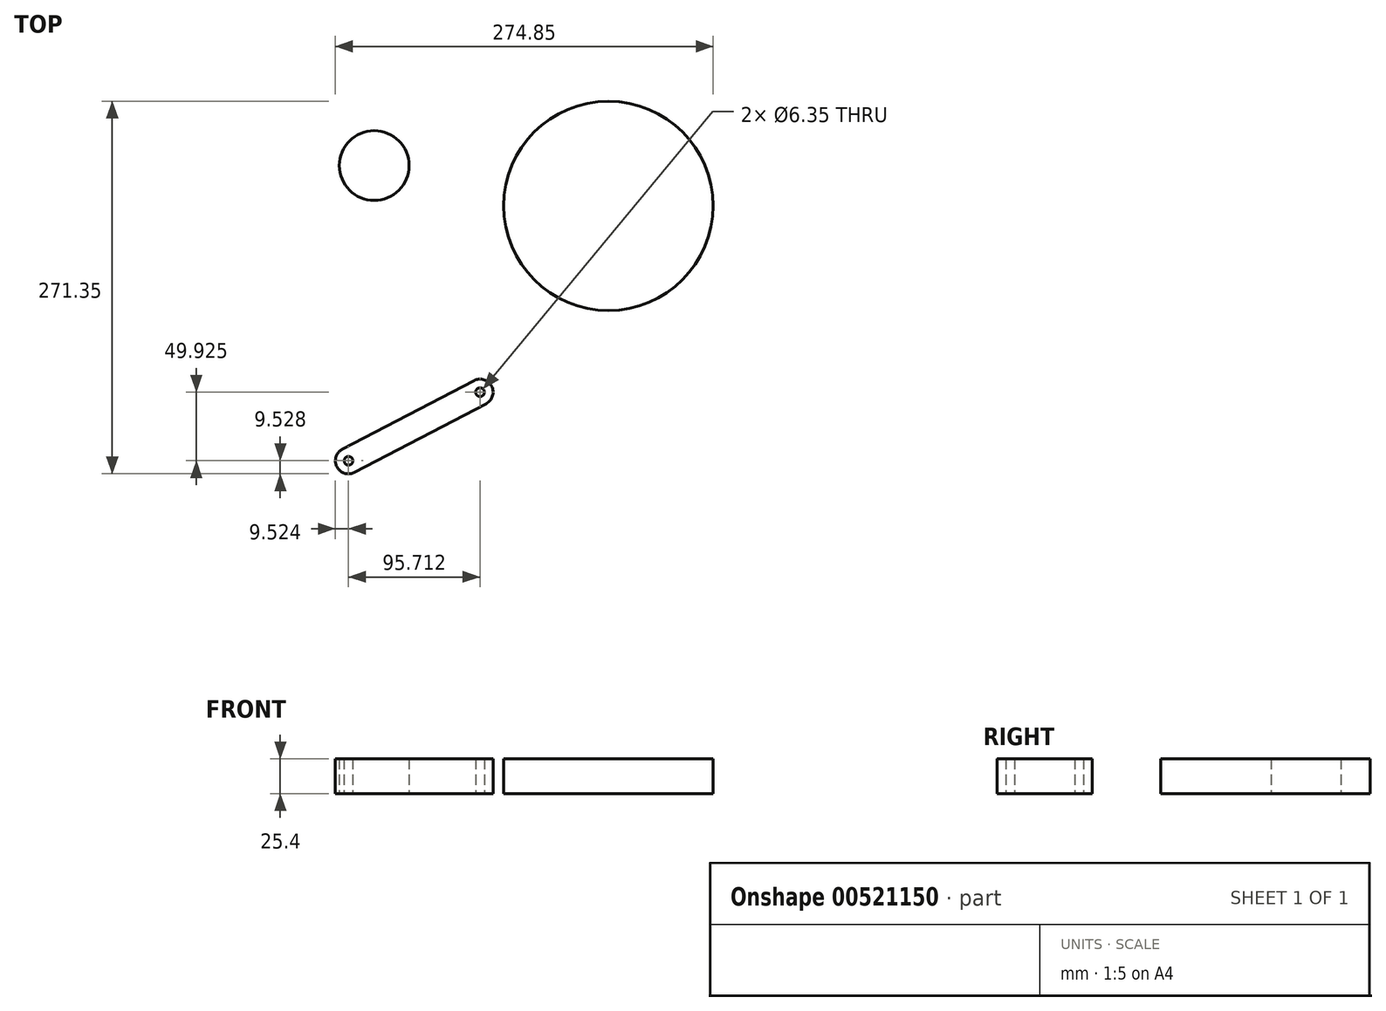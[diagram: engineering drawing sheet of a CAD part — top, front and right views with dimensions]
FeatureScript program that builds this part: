
annotation { "Feature Type Name" : "Feature", "Feature Type Description" : "" }
export const myFeature = defineFeature(function(context is Context, id is Id, definition is map)
    precondition{}
    {
        {
            var Q0;
            Q0=qCreatedBy(makeId("Top.planeOp"),FACE);
            var sketch = newSketch(context, id + "F0", { "sketchPlane" : qUnion([Q0])});
            skCircle(sketch, "E0", {"center": v(0, 0) * mm, "radius": 76.2 * mm});
            skArc(sketch, "E1", {"start": v(-14, 74.9) * mm, "mid": v(-8.35, 82.13) * mm, "end": v(-1.37, 76.19) * mm});
            skArc(sketch, "E2.1.0", {"start": v(-36.45, 66.92) * mm, "mid": v(-33.32, 75.53) * mm, "end": v(-24.84, 72.04) * mm});
            skArc(sketch, "E2.2.0", {"start": v(-55.35, 52.38) * mm, "mid": v(-55.03, 61.54) * mm, "end": v(-45.89, 60.83) * mm});
            skArc(sketch, "E3.2.3.0", {"start": v(-68.82, 32.7) * mm, "mid": v(-71.35, 41.52) * mm, "end": v(-62.44, 43.68) * mm});
            skArc(sketch, "E3.2.4.0", {"start": v(-75.56, 9.84) * mm, "mid": v(-80.69, 17.44) * mm, "end": v(-72.88, 22.24) * mm});
            skArc(sketch, "E3.2.5.0", {"start": v(-74.9, -14) * mm, "mid": v(-82.13, -8.35) * mm, "end": v(-76.19, -1.37) * mm});
            skArc(sketch, "E3.2.6.0", {"start": v(-66.92, -36.45) * mm, "mid": v(-75.53, -33.32) * mm, "end": v(-72.04, -24.84) * mm});
            skArc(sketch, "E3.2.7.0", {"start": v(-52.38, -55.35) * mm, "mid": v(-61.54, -55.03) * mm, "end": v(-60.83, -45.89) * mm});
            skArc(sketch, "E3.2.8.0", {"start": v(-32.7, -68.82) * mm, "mid": v(-41.52, -71.35) * mm, "end": v(-43.68, -62.44) * mm});
            skArc(sketch, "E3.2.9.0", {"start": v(-9.84, -75.56) * mm, "mid": v(-17.44, -80.69) * mm, "end": v(-22.24, -72.88) * mm});
            skArc(sketch, "E4.2.10.0", {"start": v(14, -74.9) * mm, "mid": v(8.35, -82.13) * mm, "end": v(1.37, -76.19) * mm});
            skArc(sketch, "E4.2.11.0", {"start": v(36.45, -66.92) * mm, "mid": v(33.32, -75.53) * mm, "end": v(24.84, -72.04) * mm});
            skArc(sketch, "E4.2.12.0", {"start": v(55.35, -52.38) * mm, "mid": v(55.03, -61.54) * mm, "end": v(45.89, -60.83) * mm});
            skArc(sketch, "E4.2.13.0", {"start": v(68.82, -32.7) * mm, "mid": v(71.35, -41.52) * mm, "end": v(62.44, -43.68) * mm});
            skArc(sketch, "E4.2.14.0", {"start": v(75.56, -9.84) * mm, "mid": v(80.69, -17.44) * mm, "end": v(72.88, -22.24) * mm});
            skArc(sketch, "E4.2.15.0", {"start": v(74.9, 14) * mm, "mid": v(82.13, 8.35) * mm, "end": v(76.19, 1.37) * mm});
            skArc(sketch, "E4.2.16.0", {"start": v(66.92, 36.45) * mm, "mid": v(75.53, 33.32) * mm, "end": v(72.04, 24.84) * mm});
            skArc(sketch, "E4.2.17.0", {"start": v(52.38, 55.35) * mm, "mid": v(61.54, 55.03) * mm, "end": v(60.83, 45.89) * mm});
            skArc(sketch, "E4.2.18.0", {"start": v(32.7, 68.82) * mm, "mid": v(41.52, 71.35) * mm, "end": v(43.68, 62.44) * mm});
            skArc(sketch, "E4.2.19.0", {"start": v(9.84, 75.56) * mm, "mid": v(17.44, 80.69) * mm, "end": v(22.24, 72.88) * mm});
            skSolve(sketch);
        }
        {
            var Q0;
            {var subQ1=sQuery(id+"F0.wireOp",EDGE,"E0");var subQ26=sQuery(id+"F0.wireOp",EDGE,"E4.2.15.0");var subQ27=makeQuery(id+"F0.imprint","INTERSECT",VERTEX,{"disambiguationData":[OD(0.0)],"derivedFrom":[subQ1,subQ26]});Q0=makeQuery(id+"F0.imprint","IMPRINT",FACE,{"disambiguationData":[TD([[makeQuery(id+"F0.imprint","IMPRINT",EDGE,{"disambiguationData":[TD([[subQ27,1.0]])],"derivedFrom":subQ1}),1.0]])]});}
            var Q1;
            {var subQ0=sQuery(id+"F0.wireOp",EDGE,"E2.2.0");Q1=makeQuery(id+"F0.imprint","IMPRINT",FACE,{"disambiguationData":[TD([[makeQuery(id+"F0.imprint","IMPRINT",EDGE,{"derivedFrom":subQ0}),-1.0]])]});}
            var Q2;
            {var subQ0=sQuery(id+"F0.wireOp",EDGE,"E3.2.3.0");Q2=makeQuery(id+"F0.imprint","IMPRINT",FACE,{"disambiguationData":[TD([[makeQuery(id+"F0.imprint","IMPRINT",EDGE,{"derivedFrom":subQ0}),-1.0]])]});}
            var Q3;
            {var subQ0=sQuery(id+"F0.wireOp",EDGE,"E3.2.4.0");Q3=makeQuery(id+"F0.imprint","IMPRINT",FACE,{"disambiguationData":[TD([[makeQuery(id+"F0.imprint","IMPRINT",EDGE,{"derivedFrom":subQ0}),-1.0]])]});}
            var Q4;
            {var subQ0=sQuery(id+"F0.wireOp",EDGE,"E3.2.5.0");Q4=makeQuery(id+"F0.imprint","IMPRINT",FACE,{"disambiguationData":[TD([[makeQuery(id+"F0.imprint","IMPRINT",EDGE,{"derivedFrom":subQ0}),-1.0]])]});}
            var Q5;
            {var subQ0=sQuery(id+"F0.wireOp",EDGE,"E3.2.6.0");Q5=makeQuery(id+"F0.imprint","IMPRINT",FACE,{"disambiguationData":[TD([[makeQuery(id+"F0.imprint","IMPRINT",EDGE,{"derivedFrom":subQ0}),-1.0]])]});}
            var Q6;
            {var subQ0=sQuery(id+"F0.wireOp",EDGE,"E3.2.7.0");Q6=makeQuery(id+"F0.imprint","IMPRINT",FACE,{"disambiguationData":[TD([[makeQuery(id+"F0.imprint","IMPRINT",EDGE,{"derivedFrom":subQ0}),-1.0]])]});}
            var Q7;
            {var subQ0=sQuery(id+"F0.wireOp",EDGE,"E3.2.8.0");Q7=makeQuery(id+"F0.imprint","IMPRINT",FACE,{"disambiguationData":[TD([[makeQuery(id+"F0.imprint","IMPRINT",EDGE,{"derivedFrom":subQ0}),-1.0]])]});}
            var Q8;
            {var subQ0=sQuery(id+"F0.wireOp",EDGE,"E3.2.9.0");Q8=makeQuery(id+"F0.imprint","IMPRINT",FACE,{"disambiguationData":[TD([[makeQuery(id+"F0.imprint","IMPRINT",EDGE,{"derivedFrom":subQ0}),-1.0]])]});}
            var Q9;
            {var subQ0=sQuery(id+"F0.wireOp",EDGE,"E4.2.10.0");Q9=makeQuery(id+"F0.imprint","IMPRINT",FACE,{"disambiguationData":[TD([[makeQuery(id+"F0.imprint","IMPRINT",EDGE,{"derivedFrom":subQ0}),-1.0]])]});}
            var Q10;
            {var subQ0=sQuery(id+"F0.wireOp",EDGE,"E4.2.11.0");Q10=makeQuery(id+"F0.imprint","IMPRINT",FACE,{"disambiguationData":[TD([[makeQuery(id+"F0.imprint","IMPRINT",EDGE,{"derivedFrom":subQ0}),-1.0]])]});}
            var Q11;
            {var subQ0=sQuery(id+"F0.wireOp",EDGE,"E4.2.12.0");Q11=makeQuery(id+"F0.imprint","IMPRINT",FACE,{"disambiguationData":[TD([[makeQuery(id+"F0.imprint","IMPRINT",EDGE,{"derivedFrom":subQ0}),-1.0]])]});}
            var Q12;
            {var subQ0=sQuery(id+"F0.wireOp",EDGE,"E4.2.13.0");Q12=makeQuery(id+"F0.imprint","IMPRINT",FACE,{"disambiguationData":[TD([[makeQuery(id+"F0.imprint","IMPRINT",EDGE,{"derivedFrom":subQ0}),-1.0]])]});}
            var Q13;
            {var subQ0=sQuery(id+"F0.wireOp",EDGE,"E4.2.14.0");Q13=makeQuery(id+"F0.imprint","IMPRINT",FACE,{"disambiguationData":[TD([[makeQuery(id+"F0.imprint","IMPRINT",EDGE,{"derivedFrom":subQ0}),-1.0]])]});}
            var Q14;
            {var subQ0=sQuery(id+"F0.wireOp",EDGE,"E4.2.15.0");Q14=makeQuery(id+"F0.imprint","IMPRINT",FACE,{"disambiguationData":[TD([[makeQuery(id+"F0.imprint","IMPRINT",EDGE,{"derivedFrom":subQ0}),-1.0]])]});}
            var Q15;
            {var subQ0=sQuery(id+"F0.wireOp",EDGE,"E4.2.16.0");Q15=makeQuery(id+"F0.imprint","IMPRINT",FACE,{"disambiguationData":[TD([[makeQuery(id+"F0.imprint","IMPRINT",EDGE,{"derivedFrom":subQ0}),-1.0]])]});}
            var Q16;
            {var subQ0=sQuery(id+"F0.wireOp",EDGE,"E4.2.17.0");Q16=makeQuery(id+"F0.imprint","IMPRINT",FACE,{"disambiguationData":[TD([[makeQuery(id+"F0.imprint","IMPRINT",EDGE,{"derivedFrom":subQ0}),-1.0]])]});}
            var Q17;
            {var subQ0=sQuery(id+"F0.wireOp",EDGE,"E4.2.18.0");Q17=makeQuery(id+"F0.imprint","IMPRINT",FACE,{"disambiguationData":[TD([[makeQuery(id+"F0.imprint","IMPRINT",EDGE,{"derivedFrom":subQ0}),-1.0]])]});}
            var Q18;
            {var subQ0=sQuery(id+"F0.wireOp",EDGE,"E4.2.19.0");Q18=makeQuery(id+"F0.imprint","IMPRINT",FACE,{"disambiguationData":[TD([[makeQuery(id+"F0.imprint","IMPRINT",EDGE,{"derivedFrom":subQ0}),-1.0]])]});}
            var Q19;
            {var subQ0=sQuery(id+"F0.wireOp",EDGE,"E1");Q19=makeQuery(id+"F0.imprint","IMPRINT",FACE,{"disambiguationData":[TD([[makeQuery(id+"F0.imprint","IMPRINT",EDGE,{"derivedFrom":subQ0}),-1.0]])]});}
            var Q20;
            {var subQ0=sQuery(id+"F0.wireOp",EDGE,"E2.1.0");Q20=makeQuery(id+"F0.imprint","IMPRINT",FACE,{"disambiguationData":[TD([[makeQuery(id+"F0.imprint","IMPRINT",EDGE,{"derivedFrom":subQ0}),-1.0]])]});}
            extrude(context, id + "F1", {"entities" : qUnion([Q0, Q1, Q2, Q3, Q4, Q5, Q6, Q7, Q8, Q9, Q10, Q11, Q12, Q13, Q14, Q15, Q16, Q17, Q18, Q19, Q20]), "depth" : 25.4 * mm});
        }
        {
            var Q0;
            Q0=qCreatedBy(makeId("Top.planeOp"),FACE);
            var sketch = newSketch(context, id + "F2", { "sketchPlane" : qUnion([Q0])});
            skCircle(sketch, "E5", {"center": v(-170.4, 29.35) * mm, "radius": 25.4 * mm});
            skArc(sketch, "E6", {"start": v(-180.02, 52.86) * mm, "mid": v(-174.76, 60.8) * mm, "end": v(-167.54, 54.59) * mm});
            skArc(sketch, "E7.1.0", {"start": v(44.23, -182.34) * mm, "mid": v(34.73, -181.75) * mm, "end": v(36.5, -172.39) * mm});
            skArc(sketch, "E7.2.0", {"start": v(135.79, 129.48) * mm, "mid": v(140.04, 120.95) * mm, "end": v(131.05, 117.8) * mm});
            skPoint(sketch, "E7.center", {"position": v(0, 0) * mm});
            skArc(sketch, "E8.1.0", {"start": v(-193.83, 39.17) * mm, "mid": v(-195.73, 48.5) * mm, "end": v(-186.23, 49.22) * mm});
            skArc(sketch, "E8.2.0", {"start": v(-193.92, 19.73) * mm, "mid": v(-201.86, 25) * mm, "end": v(-195.65, 32.22) * mm});
            skArc(sketch, "E9.2.3.0", {"start": v(-180.23, 5.93) * mm, "mid": v(-189.57, 4.03) * mm, "end": v(-190.28, 13.53) * mm});
            skArc(sketch, "E9.2.4.0", {"start": v(-160.8, 5.84) * mm, "mid": v(-166.05, -2.1) * mm, "end": v(-173.27, 4.11) * mm});
            skArc(sketch, "E9.2.5.0", {"start": v(-146.99, 19.53) * mm, "mid": v(-145.1, 10.2) * mm, "end": v(-154.59, 9.48) * mm});
            skArc(sketch, "E9.2.6.0", {"start": v(-146.9, 38.97) * mm, "mid": v(-138.96, 33.7) * mm, "end": v(-145.17, 26.48) * mm});
            skArc(sketch, "E9.2.7.0", {"start": v(-160.58, 52.77) * mm, "mid": v(-151.25, 54.67) * mm, "end": v(-150.54, 45.17) * mm});
            skSolve(sketch);
        }
        {
            var Q0;
            {var subQ1=sQuery(id+"F2.wireOp",EDGE,"E5");var subQ12=sQuery(id+"F2.wireOp",EDGE,"E9.2.6.0");var subQ13=makeQuery(id+"F2.imprint","INTERSECT",VERTEX,{"disambiguationData":[OD(0.0)],"derivedFrom":[subQ1,subQ12]});Q0=makeQuery(id+"F2.imprint","IMPRINT",FACE,{"disambiguationData":[TD([[makeQuery(id+"F2.imprint","IMPRINT",EDGE,{"disambiguationData":[TD([[subQ13,-1.0]])],"derivedFrom":subQ1}),1.0]])]});}
            var Q1;
            {var subQ0=sQuery(id+"F2.wireOp",EDGE,"E8.2.0");Q1=makeQuery(id+"F2.imprint","IMPRINT",FACE,{"disambiguationData":[TD([[makeQuery(id+"F2.imprint","IMPRINT",EDGE,{"derivedFrom":subQ0}),-1.0]])]});}
            var Q2;
            {var subQ0=sQuery(id+"F2.wireOp",EDGE,"E8.1.0");Q2=makeQuery(id+"F2.imprint","IMPRINT",FACE,{"disambiguationData":[TD([[makeQuery(id+"F2.imprint","IMPRINT",EDGE,{"derivedFrom":subQ0}),-1.0]])]});}
            var Q3;
            {var subQ0=sQuery(id+"F2.wireOp",EDGE,"E6");Q3=makeQuery(id+"F2.imprint","IMPRINT",FACE,{"disambiguationData":[TD([[makeQuery(id+"F2.imprint","IMPRINT",EDGE,{"derivedFrom":subQ0}),-1.0]])]});}
            var Q4;
            {var subQ0=sQuery(id+"F2.wireOp",EDGE,"E9.2.7.0");Q4=makeQuery(id+"F2.imprint","IMPRINT",FACE,{"disambiguationData":[TD([[makeQuery(id+"F2.imprint","IMPRINT",EDGE,{"derivedFrom":subQ0}),-1.0]])]});}
            var Q5;
            {var subQ0=sQuery(id+"F2.wireOp",EDGE,"E9.2.6.0");Q5=makeQuery(id+"F2.imprint","IMPRINT",FACE,{"disambiguationData":[TD([[makeQuery(id+"F2.imprint","IMPRINT",EDGE,{"derivedFrom":subQ0}),-1.0]])]});}
            var Q6;
            {var subQ0=sQuery(id+"F2.wireOp",EDGE,"E9.2.5.0");Q6=makeQuery(id+"F2.imprint","IMPRINT",FACE,{"disambiguationData":[TD([[makeQuery(id+"F2.imprint","IMPRINT",EDGE,{"derivedFrom":subQ0}),-1.0]])]});}
            var Q7;
            {var subQ0=sQuery(id+"F2.wireOp",EDGE,"E9.2.4.0");Q7=makeQuery(id+"F2.imprint","IMPRINT",FACE,{"disambiguationData":[TD([[makeQuery(id+"F2.imprint","IMPRINT",EDGE,{"derivedFrom":subQ0}),-1.0]])]});}
            var Q8;
            {var subQ0=sQuery(id+"F2.wireOp",EDGE,"E9.2.3.0");Q8=makeQuery(id+"F2.imprint","IMPRINT",FACE,{"disambiguationData":[TD([[makeQuery(id+"F2.imprint","IMPRINT",EDGE,{"derivedFrom":subQ0}),-1.0]])]});}
            extrude(context, id + "F3", {"entities" : qUnion([Q0, Q1, Q2, Q3, Q4, Q5, Q6, Q7, Q8]), "depth" : 25.4 * mm});
        }
        {
            var Q0;
            Q0=qCreatedBy(makeId("Top.planeOp"),FACE);
            var sketch = newSketch(context, id + "F4", { "sketchPlane" : qUnion([Q0])});
            skCircle(sketch, "E10", {"center": v(-189.13, -185.62) * mm, "radius": 3.17 * mm});
            skCircle(sketch, "E11", {"center": v(-93.41, -135.7) * mm, "radius": 3.18 * mm});
            skLineSegment(sketch, "E12", {"start": v(-193.53, -177.18) * mm, "end": v(-97.82, -127.25) * mm});
            skLineSegment(sketch, "E13", {"start": v(-184.72, -194.07) * mm, "end": v(-89, -144.14) * mm});
            skArc(sketch, "E14", {"start": v(-97.82, -127.25) * mm, "mid": v(-84.97, -131.3) * mm, "end": v(-89, -144.14) * mm});
            skArc(sketch, "E15", {"start": v(-193.53, -177.18) * mm, "mid": v(-197.57, -190.03) * mm, "end": v(-184.72, -194.07) * mm});
            skLineSegment(sketch, "E16", {"start": v(-189.13, -185.62) * mm, "end": v(-193.53, -177.18) * mm, "construction": true});
            skLineSegment(sketch, "E17", {"start": v(-189.13, -185.62) * mm, "end": v(-184.72, -194.07) * mm, "construction": true});
            skLineSegment(sketch, "E18", {"start": v(-93.41, -135.7) * mm, "end": v(-97.82, -127.25) * mm, "construction": true});
            skLineSegment(sketch, "E19", {"start": v(-93.41, -135.7) * mm, "end": v(-89, -144.14) * mm, "construction": true});
            skSolve(sketch);
        }
        {
            var Q0;
            Q0=makeQuery(id+"F4.imprint","IMPRINT",FACE,{"disambiguationData":[TD([[makeQuery(id+"F4.imprint","IMPRINT",EDGE,{"derivedFrom":sQuery(id+"F4.wireOp",EDGE,"E10")}),-1.0]])]});
            extrude(context, id + "F5", {"entities" : qUnion([Q0]), "depth" : 25.4 * mm});
        }
    });
